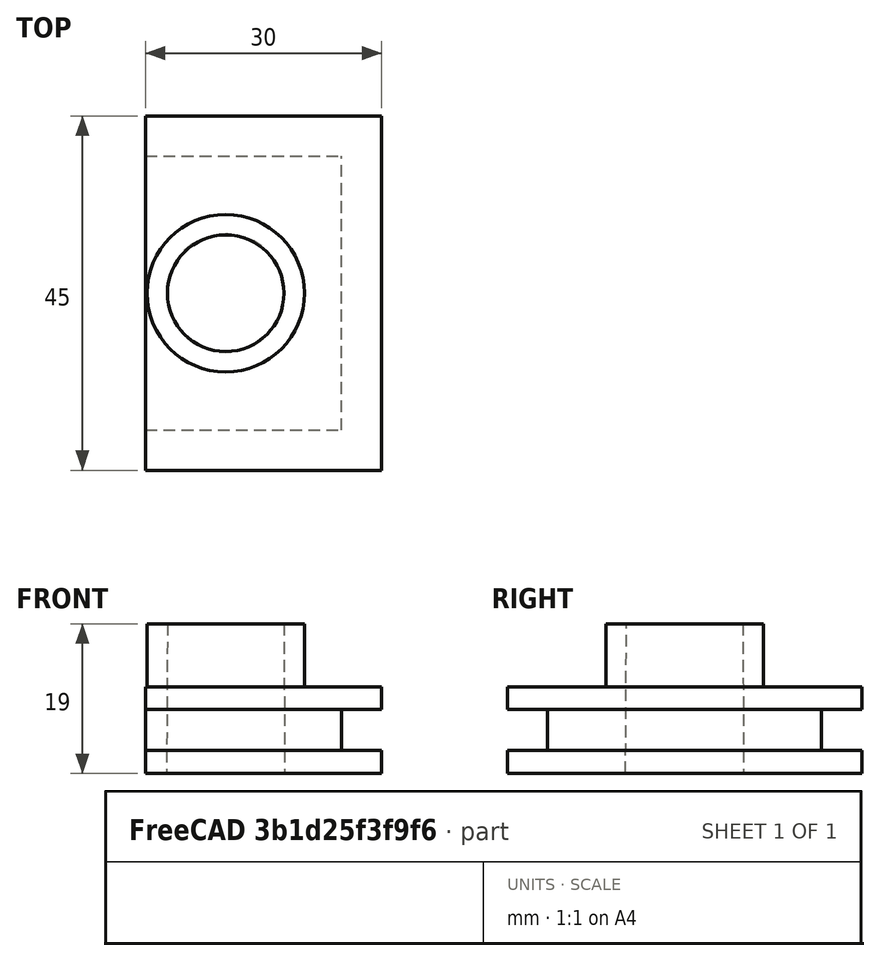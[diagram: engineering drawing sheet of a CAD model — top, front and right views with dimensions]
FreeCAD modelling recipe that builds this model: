
FCSTD DOCUMENT  (FreeCAD 0.18R16110 (Git))
Label: P1000_Adapter
License: All rights reserved
LicenseURL: http://en.wikipedia.org/wiki/All_rights_reserved
objects: Part::Box×4, Part::Cut×4, Part::Cylinder×1, Part::Cone×1, Part::MultiFuse×1, Mesh::Feature×1
note: 11 computed .brp shape members not serialized (recipe doc carries the construction recipe); baked Part::Feature solids carry a one-line shape summary decoded from their .brp

FEATURE [Part::Box] Box002  label="Quader002"
  AttacherType = Attacher::AttachEngine3D
  Height = 5.2
  Length = 5.1
  Placement = pos=(39.9,0,2.9) rot=(0,0,1;0rad)
  Width = 30
  expr: Placement.Base.x = 39.9
FEATURE [Part::Box] Box  label="Quader"
  AttacherType = Attacher::AttachEngine3D
  Height = 11
  Length = 45
  Width = 30
FEATURE [Part::Box] Box008  label="Quader008"
  AttacherType = Attacher::AttachEngine3D
  Height = 5.2
  Length = 5.1
  Placement = pos=(17.9,14.7,-0.1) rot=(0,0,1;1.5708rad)
  Width = 36
FEATURE [Part::Box] Box001  label="Quader001"
  AttacherType = Attacher::AttachEngine3D
  Height = 5.2
  Length = 5.1
  Placement = pos=(0,0,2.9) rot=(0,0,1;0rad)
  Width = 30
FEATURE [Part::Cut] Cut004
  Base = -> Box
  Tool = -> Box001
FEATURE [Part::Cut] Cut005
  Base = -> Cut004
  Placement = pos=(-22.5,-10.2,-3) rot=(0,0,1;0rad)
  Tool = -> Box002
  expr: Placement.Base.x = -45 / 2
FEATURE [Part::Cut] Cut013
  Base = -> Cut005
  Tool = -> Box008
FEATURE [Part::Cylinder] Cylinder008  label="Zylinder008"
  Angle = 360
  AttacherType = Attacher::AttachEngine3D
  Height = 19
  Placement = pos=(0,0,-3) rot=(0,0,1;0rad)
  Radius = 10
FEATURE [Part::Cone] Cone  label="Kegel"
  Angle = 360
  AttacherType = Attacher::AttachEngine3D
  Height = 19
  Placement = pos=(0,0,-3) rot=(0,0,1;0rad)
  Radius1 = 7.5
  Radius2 = 7.4
  expr: Radius2 = 14.8 / 2
  expr: Radius1 = 15 / 2
FEATURE [Part::MultiFuse] Fusion
  Shapes = -> [Cut013,Cylinder008]
FEATURE [Part::Cut] Cut014  label="Adapter"
  Base = -> Fusion
  Placement = pos=(0,0,-81) rot=(0,0,-1;1.5708rad)
  Tool = -> Cone
FEATURE [Mesh::Feature] Mesh  label="Adapter (Meshed)"
